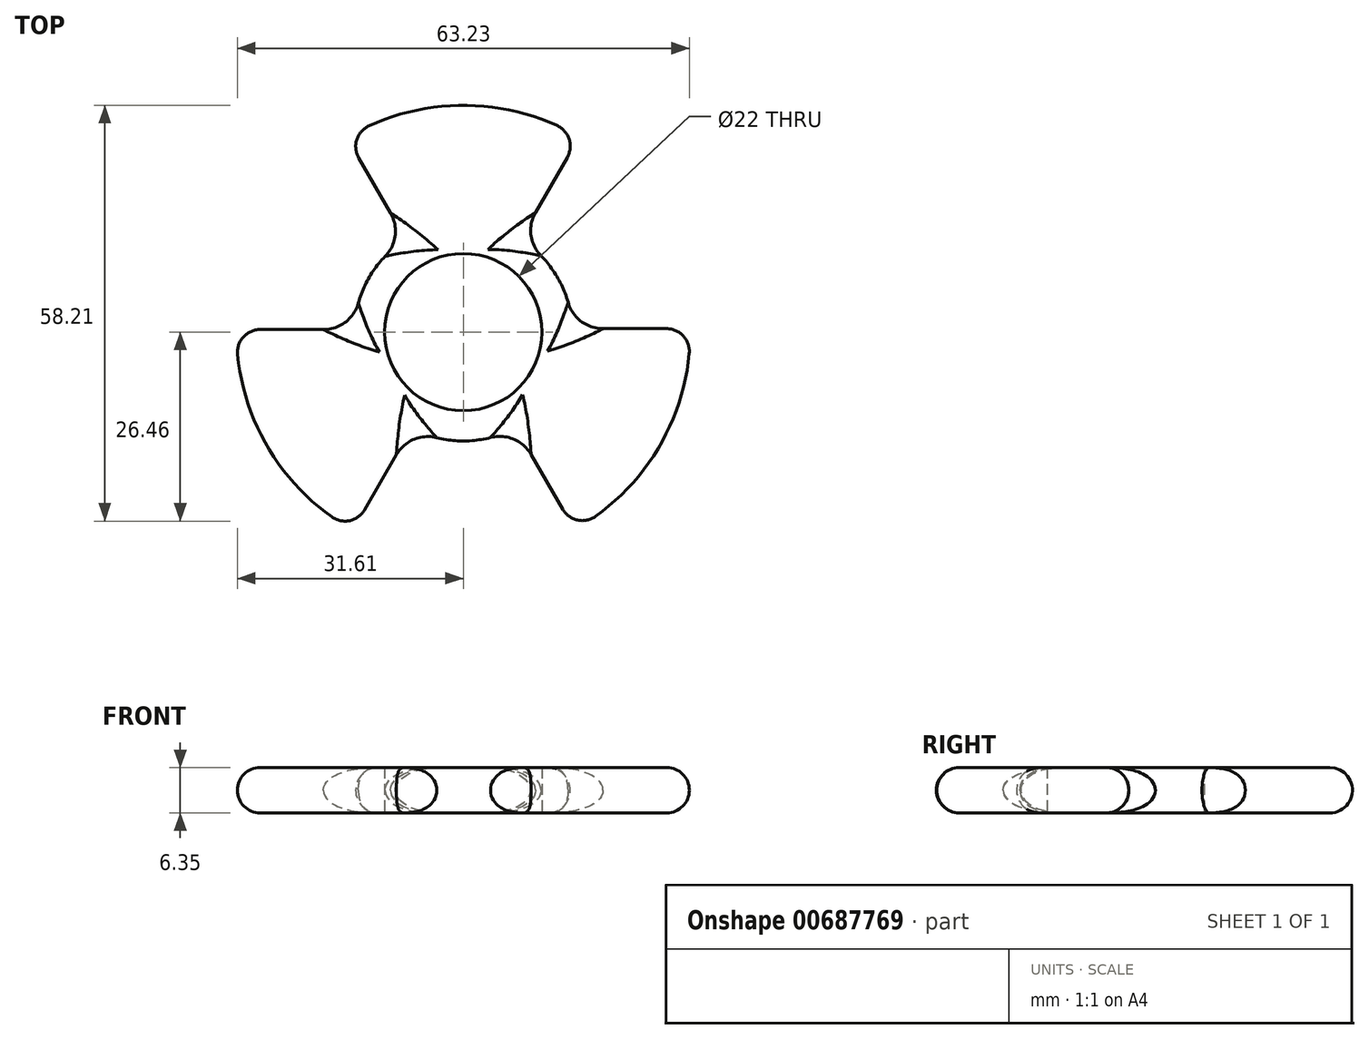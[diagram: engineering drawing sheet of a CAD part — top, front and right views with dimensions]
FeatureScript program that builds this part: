
annotation { "Feature Type Name" : "Feature", "Feature Type Description" : "" }
export const myFeature = defineFeature(function(context is Context, id is Id, definition is map)
    precondition{}
    {
        {
            var Q0;
            Q0=qCreatedBy(makeId("Top.planeOp"),FACE);
            var sketch = newSketch(context, id + "F0", { "sketchPlane" : qUnion([Q0])});
            skArc(sketch, "E0", {"start": v(16.19, 27.31) * mm, "mid": v(-0.06, 31.75) * mm, "end": v(-16.29, 27.25) * mm});
            skCircle(sketch, "E1", {"center": v(0, 0) * mm, "radius": 11 * mm});
            skLineSegment(sketch, "E2", {"start": v(-8.03, 12.95) * mm, "end": v(-16.29, 27.25) * mm});
            skLineSegment(sketch, "E3", {"start": v(7.93, 13.01) * mm, "end": v(16.19, 27.31) * mm});
            skArc(sketch, "E4.1.0", {"start": v(-7.62, -13.2) * mm, "mid": v(-0.18, -15.24) * mm, "end": v(7.3, -13.37) * mm});
            skLineSegment(sketch, "E5.1.0", {"start": v(-7.2, -13.43) * mm, "end": v(-15.46, -27.73) * mm});
            skArc(sketch, "E5.1.1", {"start": v(-31.75, 0.36) * mm, "mid": v(-27.47, -15.93) * mm, "end": v(-15.46, -27.73) * mm});
            skLineSegment(sketch, "E5.1.2", {"start": v(-15.24, 0.36) * mm, "end": v(-31.75, 0.36) * mm});
            skLineSegment(sketch, "E5.2.0", {"start": v(15.23, 0.48) * mm, "end": v(31.75, 0.48) * mm});
            skArc(sketch, "E5.2.1", {"start": v(15.56, -27.67) * mm, "mid": v(27.53, -15.82) * mm, "end": v(31.75, 0.48) * mm});
            skLineSegment(sketch, "E5.2.2", {"start": v(7.3, -13.37) * mm, "end": v(15.56, -27.67) * mm});
            skArc(sketch, "E6.trimOffspring", {"start": v(-8.03, 12.95) * mm, "mid": v(-13.23, 7.57) * mm, "end": v(-15.24, 0.36) * mm});
            skArc(sketch, "E7.trimOffspring", {"start": v(15.23, 0.48) * mm, "mid": v(13.17, 7.67) * mm, "end": v(7.93, 13.01) * mm});
            skSolve(sketch);
        }
        {
            var Q0;
            Q0=makeQuery(id+"F0.imprint","IMPRINT",FACE,{"disambiguationData":[TD([[makeQuery(id+"F0.imprint","IMPRINT",EDGE,{"derivedFrom":sQuery(id+"F0.wireOp",EDGE,"E1")}),-1.0]])]});
            var Q1;
            Q1=makeQuery(id+"F0.imprint","IMPRINT",FACE,{"disambiguationData":[TD([[makeQuery(id+"F0.imprint","IMPRINT",EDGE,{"derivedFrom":sQuery(id+"F0.wireOp",EDGE,"E0")}),1.0]])]});
            extrude(context, id + "F1", {"entities" : qUnion([Q0, Q1]), "depth" : 6.35 * mm, "offsetDistance" : 25.4 * mm});
        }
        {
            var Q0;
            Q0=makeQuery(id+"F1.opExtrude","CAP_EDGE",EDGE,{"disambiguationData":[OSD([sQuery(id+"F0.wireOp",EDGE,"E5.2.1")])],"isStart":false});
            var Q1;
            Q1=makeQuery(id+"F1.opExtrude","CAP_EDGE",EDGE,{"disambiguationData":[OSD([sQuery(id+"F0.wireOp",EDGE,"E0")])],"isStart":false});
            var Q2;
            Q2=makeQuery(id+"F1.opExtrude","CAP_EDGE",EDGE,{"disambiguationData":[OSD([sQuery(id+"F0.wireOp",EDGE,"E5.1.1")])],"isStart":false});
            var Q3;
            Q3=makeQuery(id+"F1.opExtrude","CAP_EDGE",EDGE,{"disambiguationData":[OSD([sQuery(id+"F0.wireOp",EDGE,"E0")])],"isStart":true});
            var Q4;
            Q4=makeQuery(id+"F1.opExtrude","CAP_EDGE",EDGE,{"disambiguationData":[OSD([sQuery(id+"F0.wireOp",EDGE,"E5.1.1")])],"isStart":true});
            var Q5;
            Q5=makeQuery(id+"F1.opExtrude","CAP_EDGE",EDGE,{"disambiguationData":[OSD([sQuery(id+"F0.wireOp",EDGE,"E5.2.1")])],"isStart":true});
            fillet(context, id + "F2", {"entities" : qUnion([Q0, Q1, Q2, Q3, Q4, Q5]), "radius" : 3.17 * mm, "tangentPropagation" : true, "allowEdgeOverflow" : false});
        }
        {
            var Q0;
            Q0=makeQuery(id+"F1.opExtrude","CAP_EDGE",EDGE,{"disambiguationData":[OSD([sQuery(id+"F0.wireOp",EDGE,"E7.trimOffspring")])],"isStart":false});
            var Q1;
            Q1=makeQuery(id+"F1.opExtrude","CAP_EDGE",EDGE,{"disambiguationData":[OSD([sQuery(id+"F0.wireOp",EDGE,"E6.trimOffspring")])],"isStart":false});
            var Q2;
            Q2=makeQuery(id+"F1.opExtrude","CAP_EDGE",EDGE,{"disambiguationData":[OSD([sQuery(id+"F0.wireOp",EDGE,"E4.1.0")])],"isStart":false});
            var Q3;
            Q3=makeQuery(id+"F1.opExtrude","CAP_EDGE",EDGE,{"disambiguationData":[OSD([sQuery(id+"F0.wireOp",EDGE,"E7.trimOffspring")])],"isStart":true});
            var Q4;
            Q4=makeQuery(id+"F1.opExtrude","CAP_EDGE",EDGE,{"disambiguationData":[OSD([sQuery(id+"F0.wireOp",EDGE,"E6.trimOffspring")])],"isStart":true});
            var Q5;
            Q5=makeQuery(id+"F1.opExtrude","CAP_EDGE",EDGE,{"disambiguationData":[OSD([sQuery(id+"F0.wireOp",EDGE,"E4.1.0")])],"isStart":true});
            fillet(context, id + "F3", {"entities" : qUnion([Q0, Q1, Q2, Q3, Q4, Q5]), "radius" : 3.17 * mm, "tangentPropagation" : true, "allowEdgeOverflow" : false});
        }
        {
            var Q0;
            Q0=makeQuery(id+"F1.opExtrude","CAP_EDGE",EDGE,{"disambiguationData":[OSD([sQuery(id+"F0.wireOp",EDGE,"E5.1.0")])],"isStart":false});
            var Q1;
            Q1=makeQuery(id+"F1.opExtrude","CAP_EDGE",EDGE,{"disambiguationData":[OSD([sQuery(id+"F0.wireOp",EDGE,"E5.1.0")])],"isStart":true});
            var Q2;
            Q2=makeQuery(id+"F1.opExtrude","CAP_EDGE",EDGE,{"disambiguationData":[OSD([sQuery(id+"F0.wireOp",EDGE,"E3")])],"isStart":false});
            var Q3;
            Q3=makeQuery(id+"F1.opExtrude","CAP_EDGE",EDGE,{"disambiguationData":[OSD([sQuery(id+"F0.wireOp",EDGE,"E3")])],"isStart":true});
            var Q4;
            Q4=makeQuery(id+"F1.opExtrude","CAP_EDGE",EDGE,{"disambiguationData":[OSD([sQuery(id+"F0.wireOp",EDGE,"E5.2.2")])],"isStart":false});
            var Q5;
            Q5=makeQuery(id+"F1.opExtrude","CAP_EDGE",EDGE,{"disambiguationData":[OSD([sQuery(id+"F0.wireOp",EDGE,"E5.2.0")])],"isStart":false});
            var Q6;
            Q6=makeQuery(id+"F1.opExtrude","CAP_EDGE",EDGE,{"disambiguationData":[OSD([sQuery(id+"F0.wireOp",EDGE,"E5.2.2")])],"isStart":true});
            var Q7;
            Q7=makeQuery(id+"F1.opExtrude","CAP_EDGE",EDGE,{"disambiguationData":[OSD([sQuery(id+"F0.wireOp",EDGE,"E2")])],"isStart":true});
            var Q8;
            Q8=makeQuery(id+"F1.opExtrude","CAP_EDGE",EDGE,{"disambiguationData":[OSD([sQuery(id+"F0.wireOp",EDGE,"E5.1.2")])],"isStart":false});
            fillet(context, id + "F4", {"entities" : qUnion([Q0, Q1, Q2, Q3, Q4, Q5, Q6, Q7, Q8]), "radius" : 3.17 * mm, "tangentPropagation" : true, "allowEdgeOverflow" : false});
        }
        {
            var Q0;
            Q0=makeQuery(id+"F4.opFillet","BLEND_EDGE",EDGE,{"blendedFrom":[makeQuery(id+"F1.opExtrude","CAP_EDGE",EDGE,{"disambiguationData":[OSD([sQuery(id+"F0.wireOp",EDGE,"E2")])],"isStart":false}),makeQuery(id+"F3.opFillet","BLEND_FACE",FACE,{"disambiguationData":[OSD([sQuery(id+"F0.wireOp",EDGE,"E6.trimOffspring")])]})],"blendedInto":[makeQuery(id+"F3.opFillet","BLEND_FACE",FACE,{"disambiguationData":[OSD([sQuery(id+"F0.wireOp",EDGE,"E6.trimOffspring")])]})]});
            var Q1;
            Q1=makeQuery(id+"F4.opFillet","BLEND_EDGE",EDGE,{"blendedFrom":[makeQuery(id+"F1.opExtrude","CAP_EDGE",EDGE,{"disambiguationData":[OSD([sQuery(id+"F0.wireOp",EDGE,"E5.1.0")])],"isStart":false}),makeQuery(id+"F3.opFillet","BLEND_FACE",FACE,{"disambiguationData":[OSD([sQuery(id+"F0.wireOp",EDGE,"E4.1.0")])]})],"blendedInto":[makeQuery(id+"F3.opFillet","BLEND_FACE",FACE,{"disambiguationData":[OSD([sQuery(id+"F0.wireOp",EDGE,"E4.1.0")])]})]});
            var Q2;
            Q2=makeQuery(id+"F4.opFillet","BLEND_EDGE",EDGE,{"blendedFrom":[makeQuery(id+"F1.opExtrude","CAP_EDGE",EDGE,{"disambiguationData":[OSD([sQuery(id+"F0.wireOp",EDGE,"E5.2.2")])],"isStart":false}),makeQuery(id+"F3.opFillet","BLEND_FACE",FACE,{"disambiguationData":[OSD([sQuery(id+"F0.wireOp",EDGE,"E4.1.0")])]})],"blendedInto":[makeQuery(id+"F3.opFillet","BLEND_FACE",FACE,{"disambiguationData":[OSD([sQuery(id+"F0.wireOp",EDGE,"E4.1.0")])]})]});
            var Q3;
            Q3=makeQuery(id+"F4.opFillet","BLEND_EDGE",EDGE,{"blendedFrom":[makeQuery(id+"F1.opExtrude","CAP_EDGE",EDGE,{"disambiguationData":[OSD([sQuery(id+"F0.wireOp",EDGE,"E5.2.0")])],"isStart":false}),makeQuery(id+"F3.opFillet","BLEND_FACE",FACE,{"disambiguationData":[OSD([sQuery(id+"F0.wireOp",EDGE,"E7.trimOffspring")])]})],"blendedInto":[makeQuery(id+"F3.opFillet","BLEND_FACE",FACE,{"disambiguationData":[OSD([sQuery(id+"F0.wireOp",EDGE,"E7.trimOffspring")])]})]});
            var Q4;
            Q4=makeQuery(id+"F4.opFillet","BLEND_EDGE",EDGE,{"blendedFrom":[makeQuery(id+"F1.opExtrude","CAP_EDGE",EDGE,{"disambiguationData":[OSD([sQuery(id+"F0.wireOp",EDGE,"E3")])],"isStart":false}),makeQuery(id+"F3.opFillet","BLEND_FACE",FACE,{"disambiguationData":[OSD([sQuery(id+"F0.wireOp",EDGE,"E7.trimOffspring")])]})],"blendedInto":[makeQuery(id+"F3.opFillet","BLEND_FACE",FACE,{"disambiguationData":[OSD([sQuery(id+"F0.wireOp",EDGE,"E7.trimOffspring")])]})]});
            var Q5;
            Q5=makeQuery(id+"F4.opFillet","BLEND_EDGE",EDGE,{"blendedFrom":[makeQuery(id+"F1.opExtrude","CAP_EDGE",EDGE,{"disambiguationData":[OSD([sQuery(id+"F0.wireOp",EDGE,"E5.1.2")])],"isStart":false}),makeQuery(id+"F3.opFillet","BLEND_FACE",FACE,{"disambiguationData":[OSD([sQuery(id+"F0.wireOp",EDGE,"E6.trimOffspring")])]})],"blendedInto":[makeQuery(id+"F3.opFillet","BLEND_FACE",FACE,{"disambiguationData":[OSD([sQuery(id+"F0.wireOp",EDGE,"E6.trimOffspring")])]})]});
            fillet(context, id + "F5", {"entities" : qUnion([Q0, Q1, Q2, Q3, Q4, Q5]), "radius" : 5.08 * mm, "tangentPropagation" : true, "allowEdgeOverflow" : false});
        }
    });
